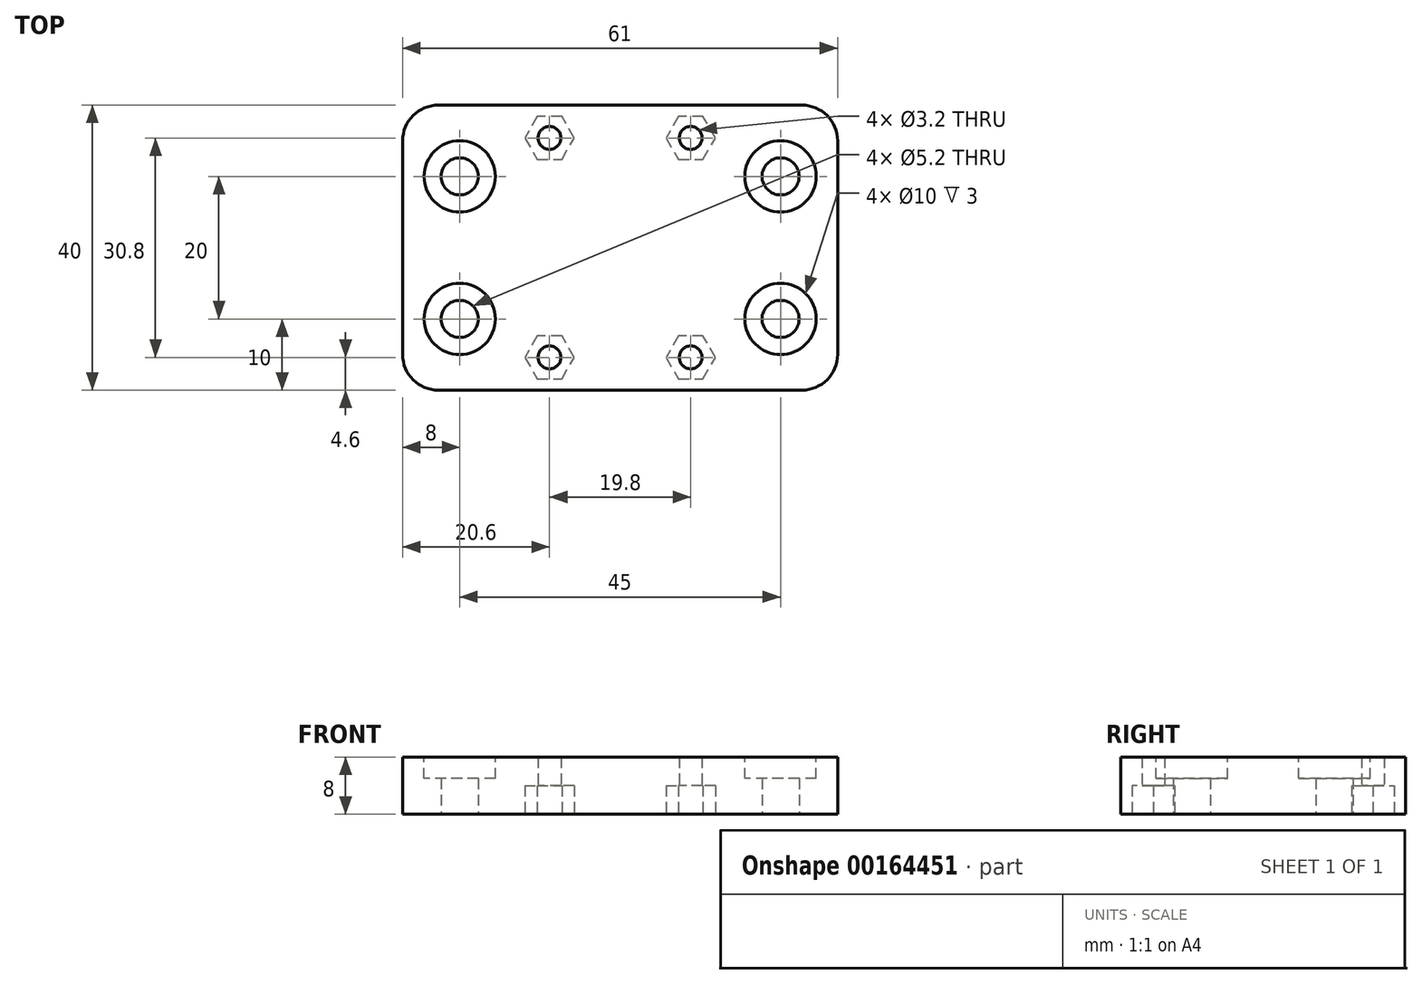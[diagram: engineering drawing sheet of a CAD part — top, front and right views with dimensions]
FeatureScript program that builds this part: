
annotation { "Feature Type Name" : "Feature", "Feature Type Description" : "" }
export const myFeature = defineFeature(function(context is Context, id is Id, definition is map)
    precondition{}
    {
        {
            var Q0;
            Q0=qCreatedBy(makeId("Top.planeOp"),FACE);
            var sketch = newSketch(context, id + "F0", { "sketchPlane" : qUnion([Q0])});
            skLineSegment(sketch, "E0.bottom", {"start": v(-30.5, 20) * mm, "end": v(30.5, 20) * mm});
            skLineSegment(sketch, "E0.top", {"start": v(-30.5, -20) * mm, "end": v(30.5, -20) * mm});
            skLineSegment(sketch, "E0.left", {"start": v(-30.5, 20) * mm, "end": v(-30.5, -20) * mm});
            skLineSegment(sketch, "E0.right", {"start": v(30.5, 20) * mm, "end": v(30.5, -20) * mm});
            skPoint(sketch, "E1", {"position": v(-30.5, 0) * mm});
            skPoint(sketch, "E2", {"position": v(0, -20) * mm});
            skCircle(sketch, "E3", {"center": v(-22.5, 10) * mm, "radius": 2.6 * mm});
            skCircle(sketch, "E4", {"center": v(-22.5, -10) * mm, "radius": 2.6 * mm});
            skCircle(sketch, "E5", {"center": v(22.5, 10) * mm, "radius": 2.6 * mm});
            skCircle(sketch, "E6", {"center": v(22.5, -10) * mm, "radius": 2.6 * mm});
            skCircle(sketch, "E7", {"center": v(-9.9, 15.4) * mm, "radius": 1.6 * mm});
            skCircle(sketch, "E8", {"center": v(9.9, 15.4) * mm, "radius": 1.6 * mm});
            skCircle(sketch, "E9", {"center": v(9.9, -15.4) * mm, "radius": 1.6 * mm});
            skCircle(sketch, "E10", {"center": v(-9.9, -15.4) * mm, "radius": 1.6 * mm});
            skSolve(sketch);
        }
        {
            var Q0;
            Q0=makeQuery(id+"F0.imprint","IMPRINT",FACE,{"disambiguationData":[TD([[makeQuery(id+"F0.imprint","IMPRINT",EDGE,{"derivedFrom":sQuery(id+"F0.wireOp",EDGE,"E0.bottom")}),-1.0]])]});
            extrude(context, id + "F1", {"entities" : qUnion([Q0]), "depth" : 8 * mm});
        }
        {
            var Q0;
            Q0=makeQuery(id+"F1.opExtrude","CAP_FACE",FACE,{"disambiguationData":[OSD([sQuery(id+"F0.wireOp",EDGE,"E0.bottom"),sQuery(id+"F0.wireOp",EDGE,"E0.top"),sQuery(id+"F0.wireOp",EDGE,"E0.left"),sQuery(id+"F0.wireOp",EDGE,"E0.right"),sQuery(id+"F0.wireOp",EDGE,"E3"),sQuery(id+"F0.wireOp",EDGE,"E4"),sQuery(id+"F0.wireOp",EDGE,"E5"),sQuery(id+"F0.wireOp",EDGE,"E6"),sQuery(id+"F0.wireOp",EDGE,"E7"),sQuery(id+"F0.wireOp",EDGE,"E8"),sQuery(id+"F0.wireOp",EDGE,"E9"),sQuery(id+"F0.wireOp",EDGE,"E10")])],"isStart":false});
            var sketch = newSketch(context, id + "F2", { "sketchPlane" : qUnion([Q0])});
            skCircle(sketch, "E11", {"center": v(-22.5, 10) * mm, "radius": 5 * mm});
            skCircle(sketch, "E12", {"center": v(-22.5, -10) * mm, "radius": 5 * mm});
            skCircle(sketch, "E13", {"center": v(22.5, -10) * mm, "radius": 5 * mm});
            skCircle(sketch, "E14", {"center": v(22.5, 10) * mm, "radius": 5 * mm});
            skSolve(sketch);
        }
        {
            var Q0;
            Q0=makeQuery(id+"F2.imprint","IMPRINT",FACE,{"disambiguationData":[TD([[makeQuery(id+"F2.imprint","IMPRINT",EDGE,{"derivedFrom":sQuery(id+"F2.wireOp",EDGE,"E11")}),1.0]])]});
            var Q1;
            Q1=makeQuery(id+"F2.imprint","IMPRINT",FACE,{"disambiguationData":[TD([[makeQuery(id+"F2.imprint","IMPRINT",EDGE,{"derivedFrom":sQuery(id+"F2.wireOp",EDGE,"E14")}),1.0]])]});
            var Q2;
            Q2=makeQuery(id+"F2.imprint","IMPRINT",FACE,{"disambiguationData":[TD([[makeQuery(id+"F2.imprint","IMPRINT",EDGE,{"derivedFrom":sQuery(id+"F2.wireOp",EDGE,"E13")}),1.0]])]});
            var Q3;
            Q3=makeQuery(id+"F2.imprint","IMPRINT",FACE,{"disambiguationData":[TD([[makeQuery(id+"F2.imprint","IMPRINT",EDGE,{"derivedFrom":sQuery(id+"F2.wireOp",EDGE,"E12")}),1.0]])]});
            extrude(context, id + "F3", {"entities" : qUnion([Q0, Q1, Q2, Q3]), "operationType" : NewBodyOperationType.REMOVE, "oppositeDirection" : true, "depth" : 3 * mm});
        }
        {
            var Q0;
            Q0=makeQuery(id+"F1.opExtrude","CAP_FACE",FACE,{"disambiguationData":[OSD([sQuery(id+"F0.wireOp",EDGE,"E0.bottom"),sQuery(id+"F0.wireOp",EDGE,"E0.top"),sQuery(id+"F0.wireOp",EDGE,"E0.left"),sQuery(id+"F0.wireOp",EDGE,"E0.right"),sQuery(id+"F0.wireOp",EDGE,"E3"),sQuery(id+"F0.wireOp",EDGE,"E4"),sQuery(id+"F0.wireOp",EDGE,"E5"),sQuery(id+"F0.wireOp",EDGE,"E6"),sQuery(id+"F0.wireOp",EDGE,"E7"),sQuery(id+"F0.wireOp",EDGE,"E8"),sQuery(id+"F0.wireOp",EDGE,"E9"),sQuery(id+"F0.wireOp",EDGE,"E10")])],"isStart":true});
            var sketch = newSketch(context, id + "F4", { "sketchPlane" : qUnion([Q0])});
            skCircle(sketch, "E15.cCircle", {"center": v(-9.9, 15.4) * mm, "radius": 3 * mm, "construction": true});
            skLineSegment(sketch, "E15.0", {"start": v(-11.63, 18.4) * mm, "end": v(-8.17, 18.4) * mm});
            skLineSegment(sketch, "E15.1", {"start": v(-8.17, 18.4) * mm, "end": v(-6.44, 15.4) * mm});
            skLineSegment(sketch, "E15.2", {"start": v(-6.44, 15.4) * mm, "end": v(-8.17, 12.4) * mm});
            skLineSegment(sketch, "E15.3", {"start": v(-8.17, 12.4) * mm, "end": v(-11.63, 12.4) * mm});
            skLineSegment(sketch, "E15.4", {"start": v(-11.63, 12.4) * mm, "end": v(-13.36, 15.4) * mm});
            skLineSegment(sketch, "E15.5", {"start": v(-13.36, 15.4) * mm, "end": v(-11.63, 18.4) * mm});
            skPoint(sketch, "E15.0.midPoint", {"position": v(-9.9, 18.4) * mm});
            skCircle(sketch, "E16.cCircle", {"center": v(9.9, 15.4) * mm, "radius": 3 * mm, "construction": true});
            skLineSegment(sketch, "E16.0", {"start": v(8.17, 18.4) * mm, "end": v(11.63, 18.4) * mm});
            skLineSegment(sketch, "E16.1", {"start": v(11.63, 18.4) * mm, "end": v(13.36, 15.4) * mm});
            skLineSegment(sketch, "E16.2", {"start": v(13.36, 15.4) * mm, "end": v(11.63, 12.4) * mm});
            skLineSegment(sketch, "E16.3", {"start": v(11.63, 12.4) * mm, "end": v(8.17, 12.4) * mm});
            skLineSegment(sketch, "E16.4", {"start": v(8.17, 12.4) * mm, "end": v(6.44, 15.4) * mm});
            skLineSegment(sketch, "E16.5", {"start": v(6.44, 15.4) * mm, "end": v(8.17, 18.4) * mm});
            skPoint(sketch, "E16.0.midPoint", {"position": v(9.9, 18.4) * mm});
            skCircle(sketch, "E17.cCircle", {"center": v(9.9, -15.4) * mm, "radius": 3 * mm, "construction": true});
            skLineSegment(sketch, "E17.0", {"start": v(11.63, -18.4) * mm, "end": v(8.17, -18.4) * mm});
            skLineSegment(sketch, "E17.1", {"start": v(8.17, -18.4) * mm, "end": v(6.44, -15.4) * mm});
            skLineSegment(sketch, "E17.2", {"start": v(6.44, -15.4) * mm, "end": v(8.17, -12.4) * mm});
            skLineSegment(sketch, "E17.3", {"start": v(8.17, -12.4) * mm, "end": v(11.63, -12.4) * mm});
            skLineSegment(sketch, "E17.4", {"start": v(11.63, -12.4) * mm, "end": v(13.36, -15.4) * mm});
            skLineSegment(sketch, "E17.5", {"start": v(13.36, -15.4) * mm, "end": v(11.63, -18.4) * mm});
            skPoint(sketch, "E17.0.midPoint", {"position": v(9.9, -18.4) * mm});
            skCircle(sketch, "E18.cCircle", {"center": v(-9.9, -15.4) * mm, "radius": 3 * mm, "construction": true});
            skLineSegment(sketch, "E18.0", {"start": v(-11.63, -12.4) * mm, "end": v(-8.17, -12.4) * mm});
            skLineSegment(sketch, "E18.1", {"start": v(-8.17, -12.4) * mm, "end": v(-6.44, -15.4) * mm});
            skLineSegment(sketch, "E18.2", {"start": v(-6.44, -15.4) * mm, "end": v(-8.17, -18.4) * mm});
            skLineSegment(sketch, "E18.3", {"start": v(-8.17, -18.4) * mm, "end": v(-11.63, -18.4) * mm});
            skLineSegment(sketch, "E18.4", {"start": v(-11.63, -18.4) * mm, "end": v(-13.36, -15.4) * mm});
            skLineSegment(sketch, "E18.5", {"start": v(-13.36, -15.4) * mm, "end": v(-11.63, -12.4) * mm});
            skPoint(sketch, "E18.0.midPoint", {"position": v(-9.9, -12.4) * mm});
            skSolve(sketch);
        }
        {
            var Q0;
            Q0=makeQuery(id+"F4.imprint","IMPRINT",FACE,{"disambiguationData":[TD([[makeQuery(id+"F4.imprint","IMPRINT",EDGE,{"derivedFrom":sQuery(id+"F4.wireOp",EDGE,"E15.0")}),-1.0]])]});
            var Q1;
            Q1=makeQuery(id+"F4.imprint","IMPRINT",FACE,{"disambiguationData":[TD([[makeQuery(id+"F4.imprint","IMPRINT",EDGE,{"derivedFrom":sQuery(id+"F4.wireOp",EDGE,"E16.0")}),-1.0]])]});
            var Q2;
            Q2=makeQuery(id+"F4.imprint","IMPRINT",FACE,{"disambiguationData":[TD([[makeQuery(id+"F4.imprint","IMPRINT",EDGE,{"derivedFrom":sQuery(id+"F4.wireOp",EDGE,"E18.0")}),-1.0]])]});
            var Q3;
            Q3=makeQuery(id+"F4.imprint","IMPRINT",FACE,{"disambiguationData":[TD([[makeQuery(id+"F4.imprint","IMPRINT",EDGE,{"derivedFrom":sQuery(id+"F4.wireOp",EDGE,"E17.0")}),-1.0]])]});
            extrude(context, id + "F5", {"entities" : qUnion([Q0, Q1, Q2, Q3]), "operationType" : NewBodyOperationType.REMOVE, "oppositeDirection" : true, "depth" : 4 * mm});
        }
        {
            var Q0;
            Q0=makeQuery(id+"F1.opExtrude","SWEPT_EDGE",EDGE,{"disambiguationData":[OSD([sQuery(id+"F0.wireOp",EDGE,"E0.bottom"),sQuery(id+"F0.wireOp",EDGE,"E0.left")])]});
            var Q1;
            Q1=makeQuery(id+"F1.opExtrude","SWEPT_EDGE",EDGE,{"disambiguationData":[OSD([sQuery(id+"F0.wireOp",EDGE,"E0.top"),sQuery(id+"F0.wireOp",EDGE,"E0.left")])]});
            var Q2;
            Q2=makeQuery(id+"F1.opExtrude","SWEPT_EDGE",EDGE,{"disambiguationData":[OSD([sQuery(id+"F0.wireOp",EDGE,"E0.top"),sQuery(id+"F0.wireOp",EDGE,"E0.right")])]});
            var Q3;
            Q3=makeQuery(id+"F1.opExtrude","SWEPT_EDGE",EDGE,{"disambiguationData":[OSD([sQuery(id+"F0.wireOp",EDGE,"E0.bottom"),sQuery(id+"F0.wireOp",EDGE,"E0.right")])]});
            fillet(context, id + "F6", {"entities" : qUnion([Q0, Q1, Q2, Q3]), "radius" : 5 * mm, "tangentPropagation" : true, "allowEdgeOverflow" : false});
        }
    });
